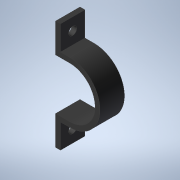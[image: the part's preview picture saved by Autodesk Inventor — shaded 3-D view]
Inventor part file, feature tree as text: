
AUTODESK INVENTOR PART (.ipt)
format: ipt  version: 2021 (Build 250183000, 183)  size: 137,728 bytes
history: native  units: mm
features: other x4, reference x3, extrude x2, sketch x2
ambient origin geometry x8: Origin, YZ Plane, XZ Plane, XY Plane, X Axis, Y Axis, Z Axis, Center Point
bodies: Volumenkörper1 (feature_tree)
feature tree (11):
  extrude  "Extrusion1"  Depth=2.4mm
  extrude  "Extrusion2"  Depth=12.5mm
  sketch  "Skizze1"  dims[d0=2.4mm d1=2.4mm]
  reference  "Referenz1"
  reference  "Referenz2"
  reference  "Referenz3"
  sketch  "Skizze2"  dims[d2=2.4mm d4=12.5mm d5=7.4mm d7=12.5mm d8=12.0mm d9=12.0mm d10=0.0mm d11=4.0mm d12=0.0mm d13=0.0mm]
  other  "<userpath>\Desktop\Bachelorarbeit\CAD\00_RobotAssembly.iam"
  other  "00_RobotAssembly.iam"
  other  "02_Motor:2"
  other  "01_CaseBottom:1"
